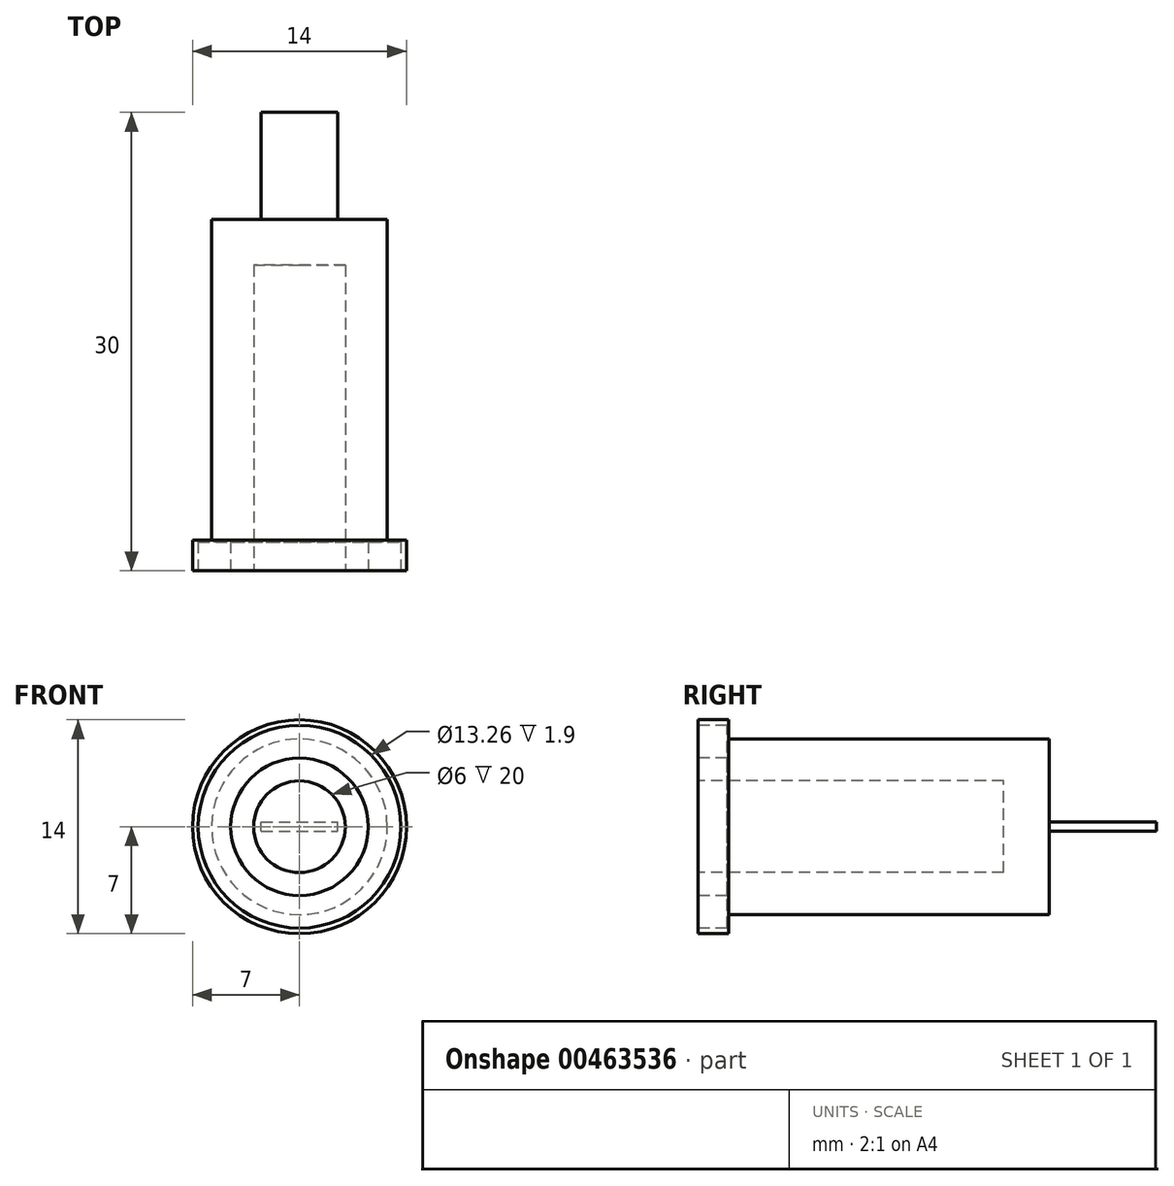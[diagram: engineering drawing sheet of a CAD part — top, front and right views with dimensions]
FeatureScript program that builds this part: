
annotation { "Feature Type Name" : "Feature", "Feature Type Description" : "" }
export const myFeature = defineFeature(function(context is Context, id is Id, definition is map)
    precondition{}
    {
        {
            var Q0;
            Q0=qCreatedBy(makeId("Front.planeOp"),FACE);
            var sketch = newSketch(context, id + "F0", { "sketchPlane" : qUnion([Q0])});
            skCircle(sketch, "E0", {"center": v(0, 0) * mm, "radius": 7 * mm});
            skSolve(sketch);
        }
        {
            var Q0;
            Q0=qSketchRegion(id+"F0",true);
            extrude(context, id + "F1", {"entities" : qUnion([Q0]), "oppositeDirection" : true, "depth" : 2 * mm, "offsetDistance" : 25 * mm});
        }
        {
            var Q0;
            Q0=makeQuery(id+"F1.opExtrude","CAP_FACE",FACE,{"disambiguationData":[OSD([sQuery(id+"F0.wireOp",EDGE,"E0")])],"isStart":false});
            var sketch = newSketch(context, id + "F2", { "sketchPlane" : qUnion([Q0])});
            skCircle(sketch, "E1", {"center": v(0, 0) * mm, "radius": 5.75 * mm});
            skSolve(sketch);
        }
        {
            var Q0;
            Q0=qSketchRegion(id+"F2",true);
            extrude(context, id + "F3", {"entities" : qUnion([Q0]), "operationType" : NewBodyOperationType.ADD, "depth" : 21 * mm, "offsetDistance" : 25 * mm});
        }
        {
            var Q0;
            Q0=makeQuery(id+"F1.opExtrude","CAP_FACE",FACE,{"disambiguationData":[OSD([sQuery(id+"F0.wireOp",EDGE,"E0")])],"isStart":true});
            var sketch = newSketch(context, id + "F4", { "sketchPlane" : qUnion([Q0])});
            skCircle(sketch, "E2", {"center": v(0, 0) * mm, "radius": 3 * mm});
            skSolve(sketch);
        }
        {
            var Q0;
            Q0=qSketchRegion(id+"F4",true);
            extrude(context, id + "F5", {"entities" : qUnion([Q0]), "operationType" : NewBodyOperationType.REMOVE, "oppositeDirection" : true, "depth" : 20 * mm, "offsetDistance" : 25 * mm});
        }
        {
            var Q0;
            Q0=makeQuery(id+"F1.opExtrude","CAP_FACE",FACE,{"disambiguationData":[OSD([sQuery(id+"F0.wireOp",EDGE,"E0")])],"isStart":true});
            var sketch = newSketch(context, id + "F6", { "sketchPlane" : qUnion([Q0])});
            skCircle(sketch, "E3", {"center": v(0, 0) * mm, "radius": 4.5 * mm});
            skCircle(sketch, "E4", {"center": v(0, 0) * mm, "radius": 6.63 * mm});
            skSolve(sketch);
        }
        {
            var Q0;
            Q0=qSketchRegion(id+"F6",true);
            extrude(context, id + "F7", {"entities" : qUnion([Q0]), "operationType" : NewBodyOperationType.REMOVE, "oppositeDirection" : true, "depth" : 1.9 * mm, "offsetDistance" : 25 * mm});
        }
        {
            var Q0;
            Q0=qCreatedBy(makeId("Top.planeOp"),FACE);
            var sketch = newSketch(context, id + "F8", { "sketchPlane" : qUnion([Q0])});
            skLineSegment(sketch, "E5.bottom", {"start": v(2.5, 22) * mm, "end": v(-2.5, 22) * mm});
            skLineSegment(sketch, "E5.top", {"start": v(2.5, 30) * mm, "end": v(-2.5, 30) * mm});
            skLineSegment(sketch, "E5.left", {"start": v(2.5, 22) * mm, "end": v(2.5, 30) * mm});
            skLineSegment(sketch, "E5.right", {"start": v(-2.5, 22) * mm, "end": v(-2.5, 30) * mm});
            skPoint(sketch, "E5.middle", {"position": v(0, 26) * mm});
            skSolve(sketch);
        }
        {
            var Q0;
            Q0=qSketchRegion(id+"F8",true);
            extrude(context, id + "F9", {"entities" : qUnion([Q0]), "operationType" : NewBodyOperationType.ADD, "depth" : .6 * mm, "offsetDistance" : 25 * mm, "symmetric" : true});
        }
    });
